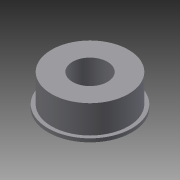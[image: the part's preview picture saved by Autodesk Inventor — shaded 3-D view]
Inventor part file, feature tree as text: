
AUTODESK INVENTOR PART (.ipt)
format: ipt  version: 2013 (Build 170138000, 138)  size: 87,552 bytes
history: native  units: in
note: dims shown in document units (in); Inventor stores cm internally (conversion verified against a paired STEP export)
features: extrude x3, sketch x3
ambient origin geometry x8: Origin, YZ Plane, XZ Plane, XY Plane, X Axis, Y Axis, Z Axis, Center Point
bodies: Solid1 (feature_tree)
feature tree (6):
  extrude  "Extrusion1"  Depth=0.0625in TaperAngle=0.0deg
  extrude  "Extrusion2"  Depth=0.5in TaperAngle=0.0deg
  extrude  "Extrusion3"  Depth=100.0in TaperAngle=0.0deg
  sketch  "Sketch1"  dims[d0=1.5in d1=0.0625in d2=0.0in]
  sketch  "Sketch2"  dims[d3=1.375in d4=0.5in d5=0.0in]
  sketch  "Sketch3"  dims[d6=0.625in d7=100.0in d8=0.0in]
